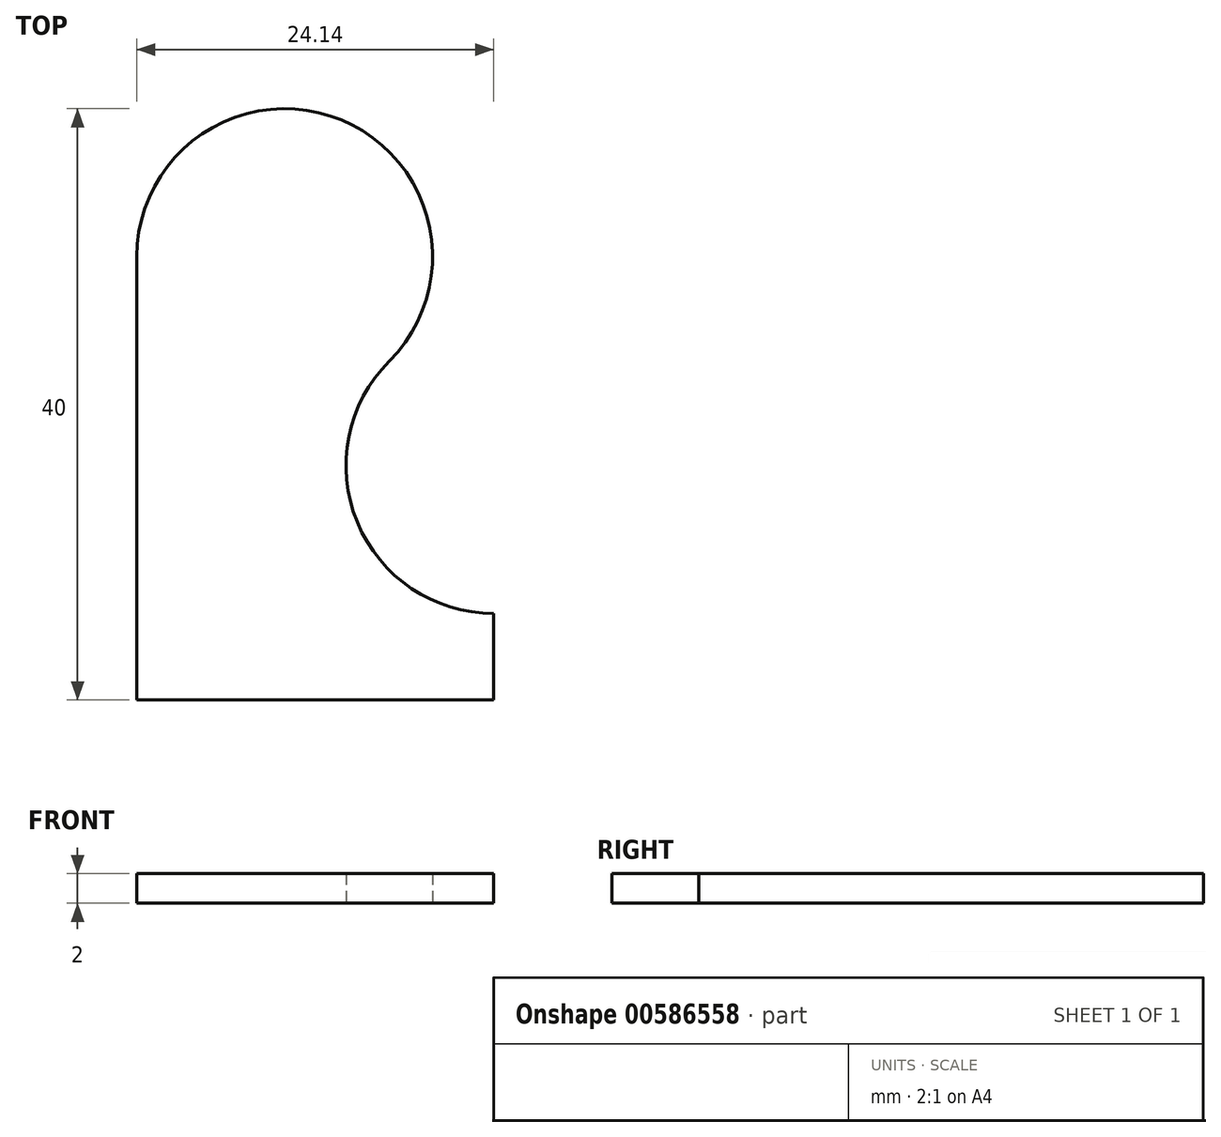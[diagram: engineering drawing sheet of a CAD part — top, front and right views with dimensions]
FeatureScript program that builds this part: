
annotation { "Feature Type Name" : "Feature", "Feature Type Description" : "" }
export const myFeature = defineFeature(function(context is Context, id is Id, definition is map)
    precondition{}
    {
        {
            var Q0;
            Q0=qCreatedBy(makeId("Top.planeOp"),FACE);
            var sketch = newSketch(context, id + "F0", { "sketchPlane" : qUnion([Q0])});
            skLineSegment(sketch, "E0", {"start": v(0, 0) * mm, "end": v(0, 30) * mm});
            skArc(sketch, "E1", {"start": v(0, 30) * mm, "mid": v(13.83, 39.24) * mm, "end": v(17.07, 22.93) * mm});
            skArc(sketch, "E2", {"start": v(17.07, 22.93) * mm, "mid": v(14.9, 12.03) * mm, "end": v(24.14, 5.86) * mm});
            skLineSegment(sketch, "E3", {"start": v(10, 30) * mm, "end": v(24.14, 15.86) * mm, "construction": true});
            skLineSegment(sketch, "E4", {"start": v(24.14, 0) * mm, "end": v(24.14, 15.86) * mm, "construction": true});
            skLineSegment(sketch, "E5", {"start": v(0, 0) * mm, "end": v(24.14, 0) * mm});
            skLineSegment(sketch, "E6", {"start": v(24.14, 5.86) * mm, "end": v(24.14, 0) * mm});
            skLineSegment(sketch, "E7", {"start": v(0, 30) * mm, "end": v(10, 30) * mm, "construction": true});
            skLineSegment(sketch, "E8", {"start": v(10, 30) * mm, "end": v(10, 20) * mm, "construction": true});
            skLineSegment(sketch, "E9", {"start": v(10, 20) * mm, "end": v(10, 10) * mm, "construction": true});
            skLineSegment(sketch, "E10", {"start": v(10, 0) * mm, "end": v(10, 10) * mm, "construction": true});
            skSolve(sketch);
        }
        {
            var Q0;
            Q0=qSketchRegion(id+"F0",true);
            extrude(context, id + "F1", {"entities" : qUnion([Q0]), "depth" : 2 * mm, "offsetDistance" : 25 * mm});
        }
    });
